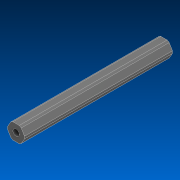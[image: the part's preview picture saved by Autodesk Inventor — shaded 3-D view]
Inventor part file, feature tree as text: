
AUTODESK INVENTOR PART (.ipt)
format: ipt  version: 2022.2 (Build 262287000, 287)  size: 125,440 bytes
history: native  units: in
note: dims shown in document units (in); Inventor stores cm internally (conversion verified against a paired STEP export)
features: extrude x1, sketch x1, other x1
ambient origin geometry x8: Origin, YZ Plane, XZ Plane, XY Plane, X Axis, Y Axis, Z Axis, Center Point
bodies: Solid1 (feature_tree)
feature tree (3):
  extrude  "Extrusion1"  TaperAngle=0.0deg  [1 undecoded]
  sketch  "Sketch1"  dims[d0=31.3in d1=0.0in]
  other  "Cut-Extrude2"
note: 1 required parameter value undecoded (feature->parameter linkage not recoverable at this tier; creation-order binding heuristic only, values carry confidence <= 0.55)
